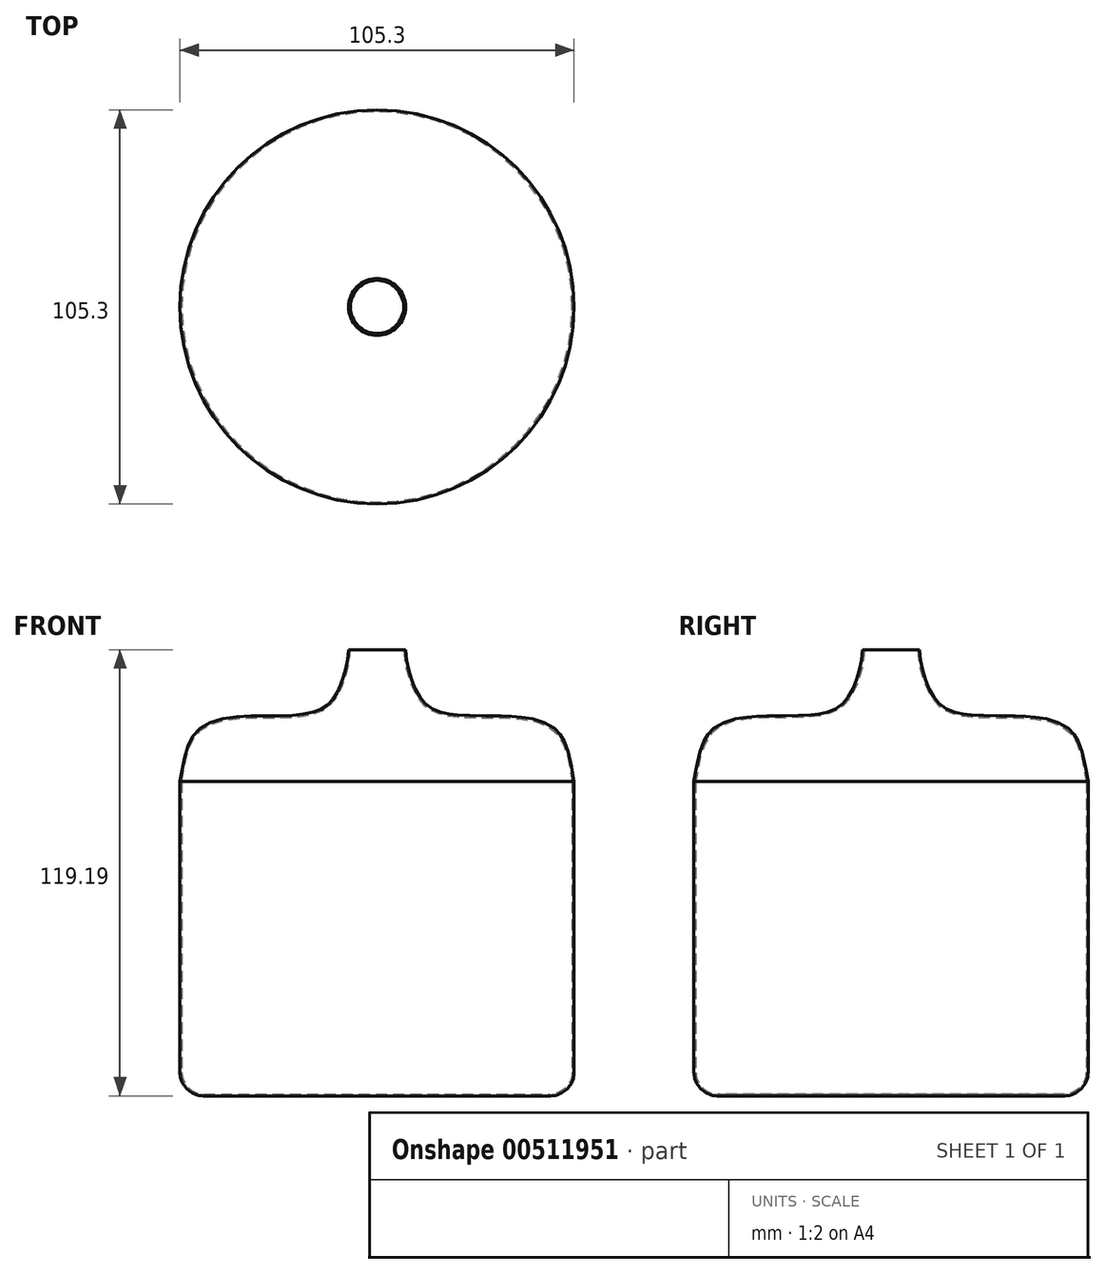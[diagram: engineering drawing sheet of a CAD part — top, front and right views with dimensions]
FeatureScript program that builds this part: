
annotation { "Feature Type Name" : "Feature", "Feature Type Description" : "" }
export const myFeature = defineFeature(function(context is Context, id is Id, definition is map)
    precondition{}
    {
        {
            var Q0;
            Q0=qCreatedBy(makeId("Front.planeOp"),FACE);
            var sketch = newSketch(context, id + "F0", { "sketchPlane" : qUnion([Q0])});
            skLineSegment(sketch, "E0", {"start": v(0, 0) * mm, "end": v(46.3, 0) * mm});
            skLineSegment(sketch, "E1", {"start": v(52.65, 6.35) * mm, "end": v(52.65, 84.06) * mm});
            skLineSegment(sketch, "E2", {"start": v(0, 0) * mm, "end": v(0, 84.06) * mm});
            skPoint(sketch, "E3.visualSharp", {"position": v(0, 0) * mm});
            skPoint(sketch, "E4.visualSharp", {"position": v(52.65, 0) * mm});
            skArc(sketch, "E4.filletArc", {"start": v(46.3, 0) * mm, "mid": v(50.79, 1.86) * mm, "end": v(52.65, 6.35) * mm});
            skFitSpline(sketch, "E5", {"points": [v(52.65, 84.06) * mm, v(47.15, 98.4) * mm, v(25.7, 101.62) * mm, v(14.04, 103.9) * mm, v(9.75, 109.8) * mm, v(7.62, 119.19) * mm], "startDerivative": vector(-12.5, 70.36) * mm, "endDerivative": vector(-3.27, 61.65) * mm});
            skLineSegment(sketch, "E6", {"start": v(7.62, 119.19) * mm, "end": v(0, 119.19) * mm});
            skLineSegment(sketch, "E7", {"start": v(0, 119.19) * mm, "end": v(0, 84.06) * mm});
            skSolve(sketch);
        }
        {
            var Q0;
            Q0 = qSketchRegion(id + "F0", true);
            var Q1;
            Q1=sQuery(id+"F0.wireOp",EDGE,"E2");
            revolve(context, id + "F1", {"entities" : qUnion([Q0]), "axis" : qUnion([Q1]), "revolveType" : RevolveType.FULL});
        }
        {
            var Q0;
            Q0=makeQuery(id+"F1.opRevolve","SWEPT_FACE",FACE,{"disambiguationData":[OSD([sQuery(id+"F0.wireOp",EDGE,"E6")])]});
            shell(context, id + "F2", {"entities" : qUnion([Q0]), "thickness" : 0.5 * mm});
        }
    });
